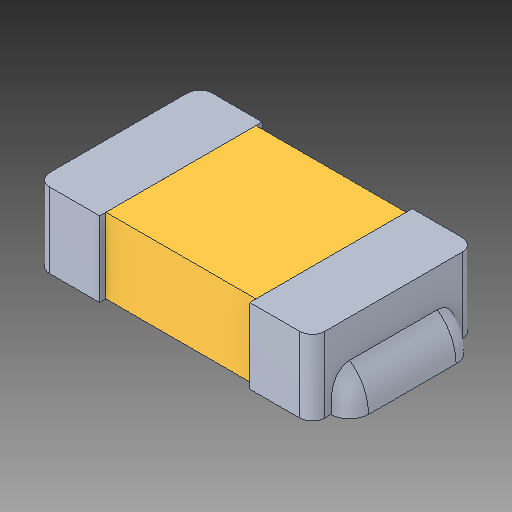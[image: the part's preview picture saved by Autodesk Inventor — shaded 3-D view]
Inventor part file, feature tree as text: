
AUTODESK INVENTOR PART (.ipt)
format: ipt  version: 2018.3 (Build 223284000, 284)  size: 160,256 bytes
history: native  units: mm
features: other x4, fillet x1, mirror x1
ambient origin geometry x8: Origin, YZ Plane, XZ Plane, XY Plane, X Axis, Y Axis, Z Axis, Center Point
bodies: Body1 (feature_tree), Body2 (feature_tree), Body3 (feature_tree)
feature tree (6):
  other  "Sólido1"
  other  "Sólido2"
  other  "Sólido3"
  other  "Boss-Extrude7"
  fillet  "Fillet5"  [1 undecoded]
  mirror  "Mirror2"
note: 1 required parameter value undecoded (feature->parameter linkage not recoverable at this tier; creation-order binding heuristic only, values carry confidence <= 0.55)
